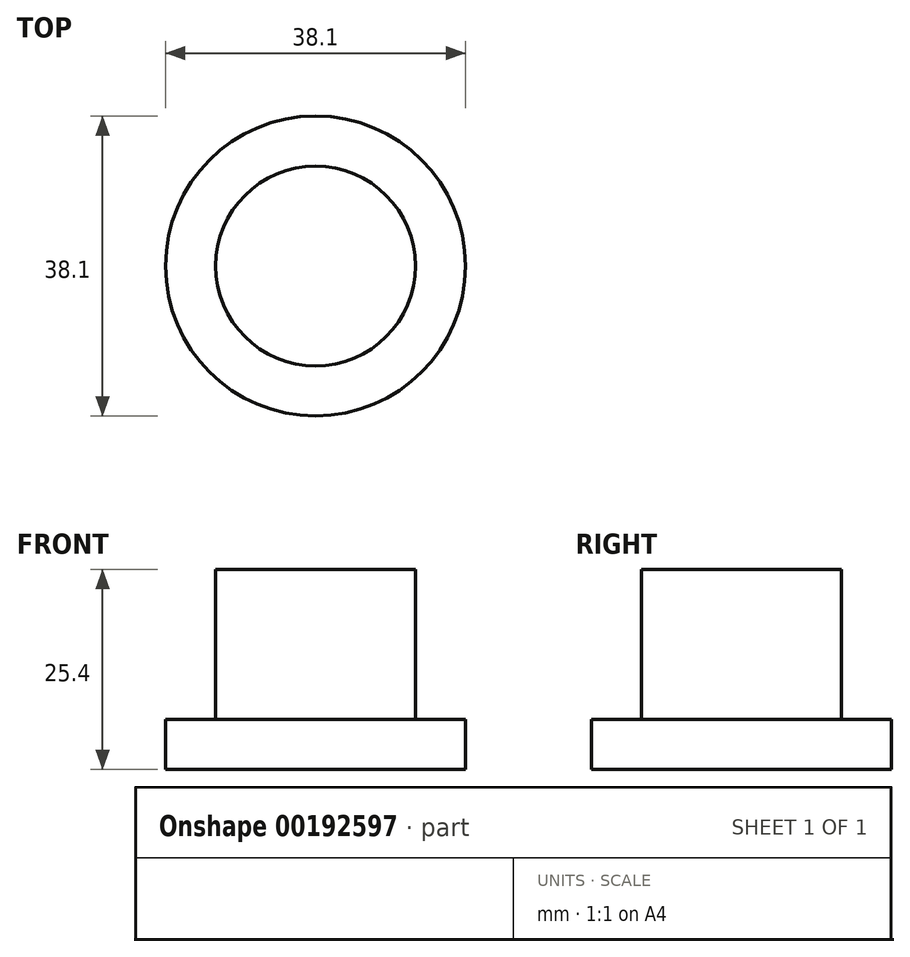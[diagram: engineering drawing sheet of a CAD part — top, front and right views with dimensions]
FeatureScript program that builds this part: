
annotation { "Feature Type Name" : "Feature", "Feature Type Description" : "" }
export const myFeature = defineFeature(function(context is Context, id is Id, definition is map)
    precondition{}
    {
        {
            var Q0;
            Q0=qCreatedBy(makeId("Top.planeOp"),FACE);
            var sketch = newSketch(context, id + "F0", { "sketchPlane" : qUnion([Q0])});
            skCircle(sketch, "E0", {"center": v(0, 0) * mm, "radius": 19.05 * mm});
            skLineSegment(sketch, "E1", {"start": v(-19.05, 0) * mm, "end": v(0, 0) * mm});
            skLineSegment(sketch, "E2", {"start": v(-4.13, 18.6) * mm, "end": v(-1.76, 12.58) * mm});
            skLineSegment(sketch, "E3.MirrorCS", {"start": v(4.13, 18.6) * mm, "end": v(1.76, 12.58) * mm});
            skArc(sketch, "E4", {"start": v(-1.76, 12.58) * mm, "mid": v(0, 11.38) * mm, "end": v(1.76, 12.58) * mm});
            skSolve(sketch);
        }
        {
            var Q0;
            Q0 = qSketchRegion(id + "F0", true);
            extrude(context, id + "F1", {"entities" : qUnion([Q0]), "depth" : 6.35 * mm});
        }
        {
            var Q0;
            {var subQ1=sQuery(id+"F0.wireOp",EDGE,"E2");Q0=makeQuery(id+"F0.imprint","IMPRINT",FACE,{"disambiguationData":[TD([[makeQuery(id+"F0.imprint","IMPRINT",EDGE,{"derivedFrom":subQ1}),-1.0]])]});}
            var sketch = newSketch(context, id + "F2", { "sketchPlane" : qUnion([Q0])});
            skCircle(sketch, "E5", {"center": v(0, 0) * mm, "radius": 12.7 * mm});
            skLineSegment(sketch, "E6", {"start": v(2.16, -12.52) * mm, "end": v(3.9, -18.58) * mm});
            skLineSegment(sketch, "E7.MirrorCS", {"start": v(-2.16, -12.52) * mm, "end": v(-3.9, -18.58) * mm});
            skArc(sketch, "E8", {"start": v(2.16, -12.52) * mm, "mid": v(0, -10.9) * mm, "end": v(-2.16, -12.52) * mm});
            skSolve(sketch);
        }
        {
            var Q0;
            Q0 = qSketchRegion(id + "F2", true);
            extrude(context, id + "F3", {"entities" : qUnion([Q0]), "operationType" : NewBodyOperationType.ADD, "depth" : 25.4 * mm});
        }
    });
